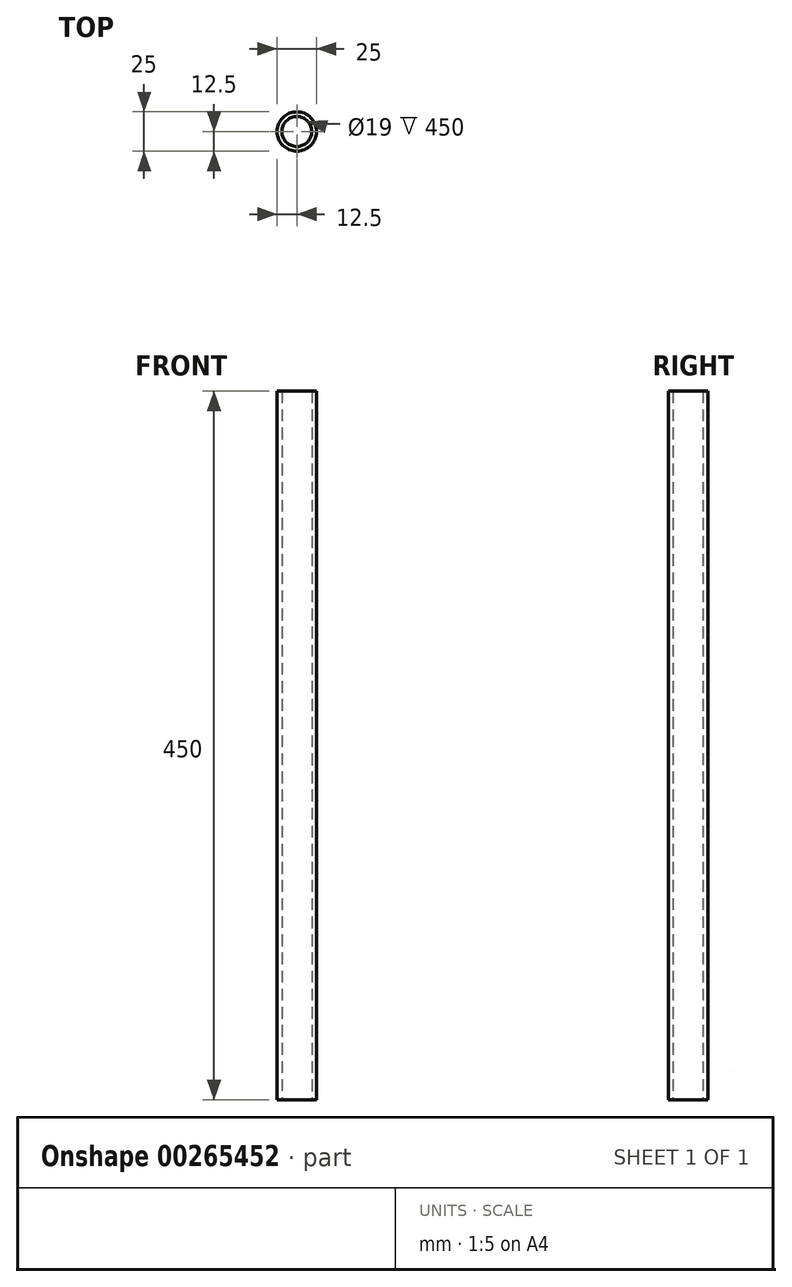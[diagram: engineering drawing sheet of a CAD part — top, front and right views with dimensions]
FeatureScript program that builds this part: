
annotation { "Feature Type Name" : "Feature", "Feature Type Description" : "" }
export const myFeature = defineFeature(function(context is Context, id is Id, definition is map)
    precondition{}
    {
        {
            var Q0;
            Q0=qCreatedBy(makeId("Top.planeOp"),FACE);
            var sketch = newSketch(context, id + "F0", { "sketchPlane" : qUnion([Q0])});
            skCircle(sketch, "E0", {"center": v(0, 0) * mm, "radius": 12.5 * mm});
            skCircle(sketch, "E1", {"center": v(0, 0) * mm, "radius": 9.5 * mm});
            skSolve(sketch);
        }
        {
            var Q0;
            Q0 = qSketchRegion(id + "F0", true);
            extrude(context, id + "F1", {"entities" : qUnion([Q0]), "endBound" : BoundingType.SYMMETRIC, "depth" : 450 * mm});
        }
    });
